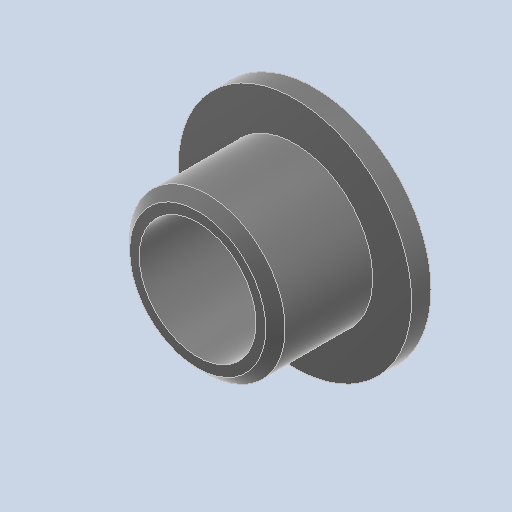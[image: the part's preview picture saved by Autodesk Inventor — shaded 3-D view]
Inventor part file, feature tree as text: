
AUTODESK INVENTOR PART (.ipt)
format: ipt  version: 2023 (Build 270158000, 158)  size: 128,512 bytes
history: native  units: mm
features: other x3, sketch x2
ambient origin geometry x8: Origin, YZ Plane, XZ Plane, XY Plane, X Axis, Y Axis, Z Axis, Center Point
bodies: Solid1 (feature_tree)
feature tree (5):
  other  "w5f6-8a.ipt"
  other  "Solid1::w5f6-8a.ipt"
  other  "TaggingFeature1"
  sketch  "Sketch1"  dims[d0=10.0mm]
  sketch  "Sketch2"
